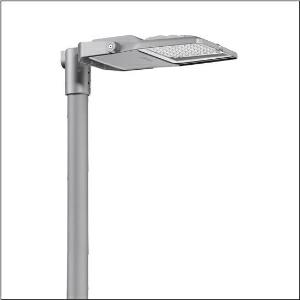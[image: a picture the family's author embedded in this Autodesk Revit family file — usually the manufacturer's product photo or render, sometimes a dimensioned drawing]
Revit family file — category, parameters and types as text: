
# Revit family: floodlight_fl_21_iq_mini___pl64_5xa7771d4e3a_aa37
name_source: partatom
category: Lighting Fixtures
units: mm (PartAtom-declared; Revit-internal decimal feet)

## family parameters
Cut with Voids When Loaded = No
Host = Face
Light Source = No
Part Type = Normal
Room Calculation Point = No
Round Connector Dimension = Use Diameter
Shared = No

## types (1)
- --- (1 x LED, 17970 lm, 143 W, 4000K)
    Apparent Load = 143 VA
    CIE Flux Codes = 28 80 98 100 100
    Color Rendering = 70
    Color Temperature = 4000K
    Default Elevation = 1800 mm
    Description = Floodlight FL 21 iQ mini, floodlight, primary light control with lens, of PMMA, primary optical cover: protective disc, of toughened safety glass, transparent, light distribution: PL64, light emission: direct distribution, installation type: surface-mounted, lamps: LED, High Power LED, rated values: 17.970lm | 143W | 125,7lm/W (begin service life); end service life: 17.970lm | 151,6W; at 50% lumin. flux: 8.985lm | 60,8W | 147,8lm/W, colour temperature: 4000K, colour rendering: CRI > 70, light colour: 740, light setting 1 begin service life: 100% | 17.970lm | 143W | 125,7lm/W | 4.000K, light setting 1 end service life: 151,6W, further light settings possible, control: Auto-Match, Temp-Guard, Lumen-Switch, Night-Set, Smart-Wire, Light-Fading, Desk-Remote (wireless, voltage-free reading and setting of iQ features in the workshop via application-optimized NFC function/RFID function), optimised constant luminous flux control (CLO 2.0), pre-setting: linear dimming characteristic, with terminal, 6-pole, mains connection: 220..240V, AC, 50/60Hz, luminaire housing, of diecast aluminium, powder-coated, SITECO metallic grey (DB 702S), corrosivity category C5 mid according to DIN EN ISO 12944suitable for swimming poolschlorine-resistant, sealing non-destructively replaceable, please order mast flange separately, mast bracket, of steel, galvanised, powder-coated, SITECO metallic grey (DB 702S), protection rating (complete): IP66, insulation class (complete): insulation class II (safety insulation), certification: CE, ENEC, VDE, protection symbol: D, impact resistance: IK08, permissible operating ambient temperature: -40..+40°C, permissible operating ambient temperature for outdoor applications: -40..+50°C, standard: DIN EN 12944, LABS conformity tested according to VDMA 24364:2018-05, packaging unit: 1 piece

Light Distribution: PL64
    Height = 70 mm
    Lamp = 1 x LED
    Lamp Light Flux = 17970 lm
    Lamp Power = 143 W
    Lamp count = 1
    Length = 485 mm
    Luminous efficacy = 126 lm/W
    Manufacturer = Siteco
    ModVariant = No
    Model = 5XA7771D4E3A
    Mounting Place = Pole
    Mounting Type = Pole annexe
    Number of Poles = 1
    OnlyDefault = Yes
    Power Factor = 1
    Product Name = Floodlight FL 21 iQ mini | PL64
    Product group = floodlight | pylon annexe
    ProductGroupID = 6201
    Protection Class = Protection class II
    Protection Degree = IP 66
    RLX_Detail_Level = 1
    RLX_Emergency_Light_Flux = 0 lm
    RLX_Emergency_Type = 0
    RLX_Emergency_Type_DB = No
    RlxData = <blob elided: 101897 chars, md5=7360ae66>
    Socket = socket
    Standby Power = 0 W
    System Light Flux = 17970 lm
    System Power = 143 W
    Type Comments = factory setting: luminous flux: 100 % | dim-lin: 254 | 730 mA
    Type Image = l_1007125.jpg
    URL = http://relux.com
    VarID = @adj_166987
    Voltage = 0 V
    Weight = 0.00 kg
    Width = 337 mm

## geometry (parser evidence)
native form markers: Blend x4, Sweep x13
no freeform markers — native parametric forms only
